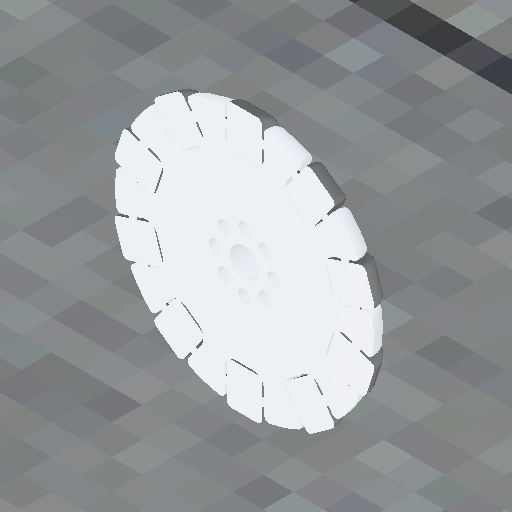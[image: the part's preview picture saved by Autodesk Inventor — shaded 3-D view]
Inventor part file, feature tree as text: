
AUTODESK INVENTOR PART (.ipt)
format: ipt  version: 2017 (Build 210142000, 142)  size: 888,320 bytes
history: native  units: in
note: dims shown in document units (in); Inventor stores cm internally (conversion verified against a paired STEP export)
features: sketch x8, extrude x4, fillet x4, pattern_circular x3, split x2, hole x1, revolve x1
ambient origin geometry x8: Origin, YZ Plane, XZ Plane, XY Plane, X Axis, Y Axis, Z Axis, Center Point
bodies: Solid1 (feature_tree)
feature tree (23):
  extrude  "Extrusion1"  Depth=0.4in TaperAngle=0.0deg
  fillet  "Fillet1"  Radius=0.175in
  extrude  "Extrusion2"  Depth=0.5in TaperAngle=0.0deg
  hole  "Hole1"  [1 undecoded]
  pattern_circular  "Circular Pattern1"  [2 undecoded]
  extrude  "Extrusion3"  Depth=0.05in
  fillet  "Fillet2"  Radius=0.125in
  extrude  "Extrusion4"  Depth=0.05in
  fillet  "Fillet3"  Radius=3.937in
  split  "Split1"
  fillet  "Fillet4"  Radius=1.4in
  pattern_circular  "Circular Pattern2"  [2 undecoded]
  split  "Split2"
  revolve  "Revolution1"  [1 undecoded]
  pattern_circular  "Circular Pattern3"  Angle=180.0deg  [1 undecoded]
  sketch  "Sketch1"  dims[d0=2.8in d1=0.4in d2=0.0in d3=0.175in]
  sketch  "Sketch2"  dims[d4=0.175in d8=0.5in d9=0.0in]
  sketch  "Sketch3"  dims[d11=0.137in d12=0.75in d13=0.375in d14=0.25in d15=0.5635in d16=1.0in d17=0.8108in d18=3.1496in d19=360.0deg]
  sketch  "Sketch4"  dims[d21=1.75in]
  sketch  "Sketch5"  dims[d22=0.05in d23=0.0in]
  sketch  "Sketch6"  dims[d24=0.05in]
  sketch  "Sketch7"  dims[d25=1.75in]
  sketch  "Sketch8"  dims[d26=0.05in d27=0.0in d28=0.05in d31=2.8in d32=0.125in d33=0.05in d34=3.937in d35=360.0deg d37=1.4in d38=1.4in d39=0.05in d40=180.0deg d41=3.937in d42=360.0deg]
note: 7 required parameter values undecoded (feature->parameter linkage not recoverable at this tier; creation-order binding heuristic only, values carry confidence <= 0.55)